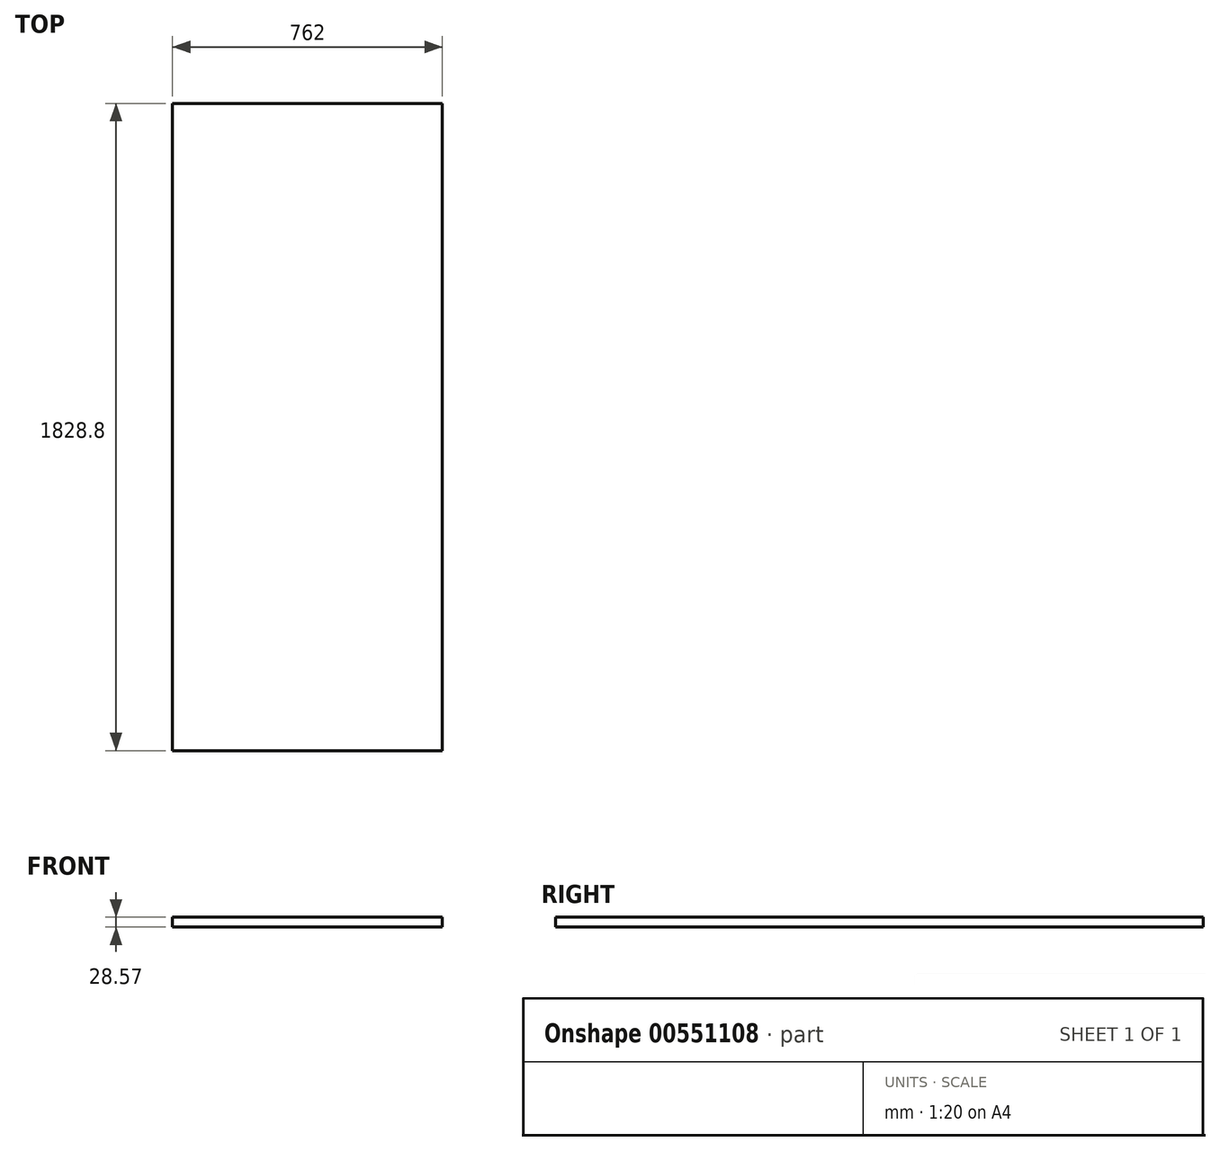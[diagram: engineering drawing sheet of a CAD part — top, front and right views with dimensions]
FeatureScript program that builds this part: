
annotation { "Feature Type Name" : "Feature", "Feature Type Description" : "" }
export const myFeature = defineFeature(function(context is Context, id is Id, definition is map)
    precondition{}
    {
        {
            var Q0;
            Q0=qCreatedBy(makeId("Top.planeOp"),FACE);
            var sketch = newSketch(context, id + "F0", { "sketchPlane" : qUnion([Q0])});
            skLineSegment(sketch, "E0.bottom", {"start": v(381, 914.4) * mm, "end": v(-381, 914.4) * mm});
            skLineSegment(sketch, "E0.top", {"start": v(381, -914.4) * mm, "end": v(-381, -914.4) * mm});
            skLineSegment(sketch, "E0.left", {"start": v(381, 914.4) * mm, "end": v(381, -914.4) * mm});
            skLineSegment(sketch, "E0.right", {"start": v(-381, 914.4) * mm, "end": v(-381, -914.4) * mm});
            skPoint(sketch, "E0.middle", {"position": v(0, 0) * mm});
            skSolve(sketch);
        }
        {
            var Q0;
            Q0=makeQuery(id+"F0.imprint","IMPRINT",FACE,{"disambiguationData":[TD([[makeQuery(id+"F0.imprint","IMPRINT",EDGE,{"derivedFrom":sQuery(id+"F0.wireOp",EDGE,"E0.bottom")}),1.0]])]});
            extrude(context, id + "F1", {"entities" : qUnion([Q0]), "depth" : 28.57 * mm, "offsetDistance" : 25.4 * mm});
        }
    });
